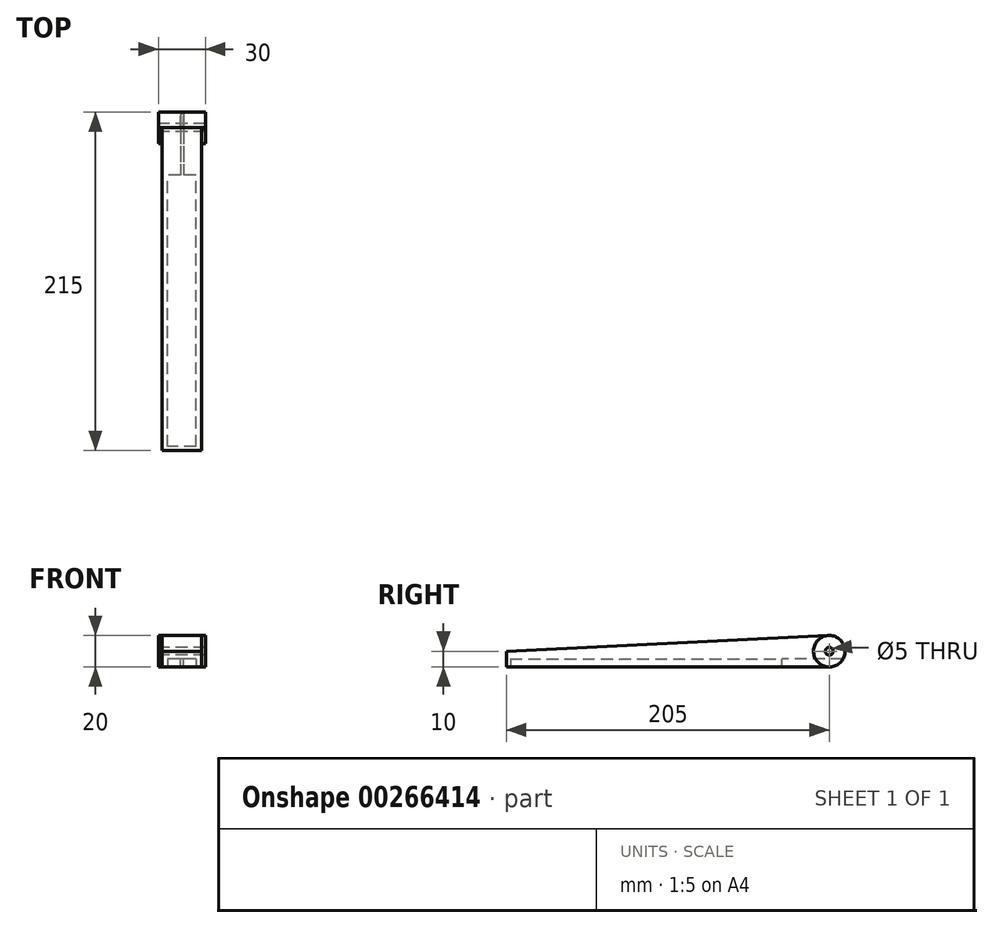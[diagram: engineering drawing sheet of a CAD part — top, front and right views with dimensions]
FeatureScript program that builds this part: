
annotation { "Feature Type Name" : "Feature", "Feature Type Description" : "" }
export const myFeature = defineFeature(function(context is Context, id is Id, definition is map)
    precondition{}
    {
        {
            var Q0;
            Q0=qCreatedBy(makeId("Right.planeOp"),FACE);
            var sketch = newSketch(context, id + "F0", { "sketchPlane" : qUnion([Q0])});
            skCircle(sketch, "E0", {"center": v(97.5, 0) * mm, "radius": 10 * mm});
            skLineSegment(sketch, "E1", {"start": v(97.5, 10) * mm, "end": v(-107.5, 0) * mm});
            skCircle(sketch, "E2", {"center": v(97.5, 0) * mm, "radius": 2.5 * mm});
            skLineSegment(sketch, "E3", {"start": v(97.5, -10) * mm, "end": v(-107.5, -10) * mm});
            skLineSegment(sketch, "E4", {"start": v(-107.5, 0) * mm, "end": v(-107.5, -10) * mm});
            skSolve(sketch);
        }
        {
            var Q0;
            Q0=makeQuery(id+"F0.imprint","IMPRINT",FACE,{"disambiguationData":[TD([[makeQuery(id+"F0.imprint","IMPRINT",EDGE,{"derivedFrom":sQuery(id+"F0.wireOp",EDGE,"E2")}),-1.0]])]});
            extrude(context, id + "F1", {"entities" : qUnion([Q0]), "depth" : 15 * mm, "hasSecondDirection" : true, "secondDirectionOppositeDirection" : true, "secondDirectionDepth" : 15 * mm, "offsetDistance" : 25 * mm});
        }
        {
            var Q0;
            {var subQ0=sQuery(id+"F0.wireOp",EDGE,"E3");Q0=makeQuery(id+"F0.imprint","IMPRINT",FACE,{"disambiguationData":[TD([[makeQuery(id+"F0.imprint","IMPRINT",EDGE,{"derivedFrom":subQ0}),-1.0]])]});}
            extrude(context, id + "F2", {"entities" : qUnion([Q0]), "operationType" : NewBodyOperationType.ADD, "depth" : 12.5 * mm, "hasSecondDirection" : true, "secondDirectionOppositeDirection" : true, "secondDirectionDepth" : 12.5 * mm, "offsetDistance" : 25 * mm});
        }
        {
            var Q0;
            Q0=makeQuery(id+"F2.opExtrude","SWEPT_FACE",FACE,{"disambiguationData":[OSD([sQuery(id+"F0.wireOp",EDGE,"E3")])]});
            var sketch = newSketch(context, id + "F3", { "sketchPlane" : qUnion([Q0])});
            skLineSegment(sketch, "E5", {"start": v(9, 105) * mm, "end": v(-9, 105) * mm});
            skLineSegment(sketch, "E6", {"start": v(-9, 105) * mm, "end": v(-9, -95) * mm});
            skLineSegment(sketch, "E7", {"start": v(9, 105) * mm, "end": v(9, -95) * mm});
            skLineSegment(sketch, "E8", {"start": v(9, -95) * mm, "end": v(-9, -95) * mm});
            skLineSegment(sketch, "E9", {"start": v(0, -95) * mm, "end": v(0, -67.5) * mm, "construction": true});
            skLineSegment(sketch, "E10", {"start": v(0, -67.5) * mm, "end": v(9, -67.5) * mm});
            skLineSegment(sketch, "E11", {"start": v(0, -67.5) * mm, "end": v(-9, -67.5) * mm});
            skSolve(sketch);
        }
        {
            var Q0;
            Q0=makeQuery(id+"F3.imprint","IMPRINT",FACE,{"disambiguationData":[TD([[makeQuery(id+"F3.imprint","IMPRINT",EDGE,{"derivedFrom":sQuery(id+"F3.wireOp",EDGE,"E5")}),1.0]])]});
            extrude(context, id + "F4", {"entities" : qUnion([Q0]), "operationType" : NewBodyOperationType.REMOVE, "oppositeDirection" : true, "depth" : 5 * mm});
        }
        {
            var Q0;
            Q0=makeQuery(id+"F4.boolean.opBoolean","COPY",FACE,{"derivedFrom":makeQuery(id+"F4.opExtrude","SWEPT_FACE",FACE,{"disambiguationData":[OSD([sQuery(id+"F3.wireOp",EDGE,"E10"),sQuery(id+"F3.wireOp",EDGE,"E11")])]})});
            var sketch = newSketch(context, id + "F5", { "sketchPlane" : qUnion([Q0])});
            skLineSegment(sketch, "E12", {"start": v(0, -5) * mm, "end": v(0, -10) * mm, "construction": true});
            skLineSegment(sketch, "E13", {"start": v(0, -10) * mm, "end": v(-1, -10) * mm});
            skLineSegment(sketch, "E14", {"start": v(0, -10) * mm, "end": v(1, -10) * mm});
            skLineSegment(sketch, "E15", {"start": v(-1, -10) * mm, "end": v(-1, -5) * mm});
            skLineSegment(sketch, "E16", {"start": v(-1, -5) * mm, "end": v(0, -5) * mm});
            skLineSegment(sketch, "E17", {"start": v(1, -10) * mm, "end": v(1, -5) * mm});
            skLineSegment(sketch, "E18", {"start": v(1, -5) * mm, "end": v(0, -5) * mm});
            skSolve(sketch);
        }
        {
            var Q0;
            Q0=makeQuery(id+"F5.imprint","IMPRINT",FACE,{"disambiguationData":[TD([[makeQuery(id+"F5.imprint","IMPRINT",EDGE,{"derivedFrom":sQuery(id+"F5.wireOp",EDGE,"E13")}),-1.0]])]});
            extrude(context, id + "F6", {"entities" : qUnion([Q0]), "operationType" : NewBodyOperationType.REMOVE, "endBound" : BoundingType.THROUGH_ALL, "oppositeDirection" : true, "depth" : 25 * mm, "offsetDistance" : 25 * mm});
        }
    });
